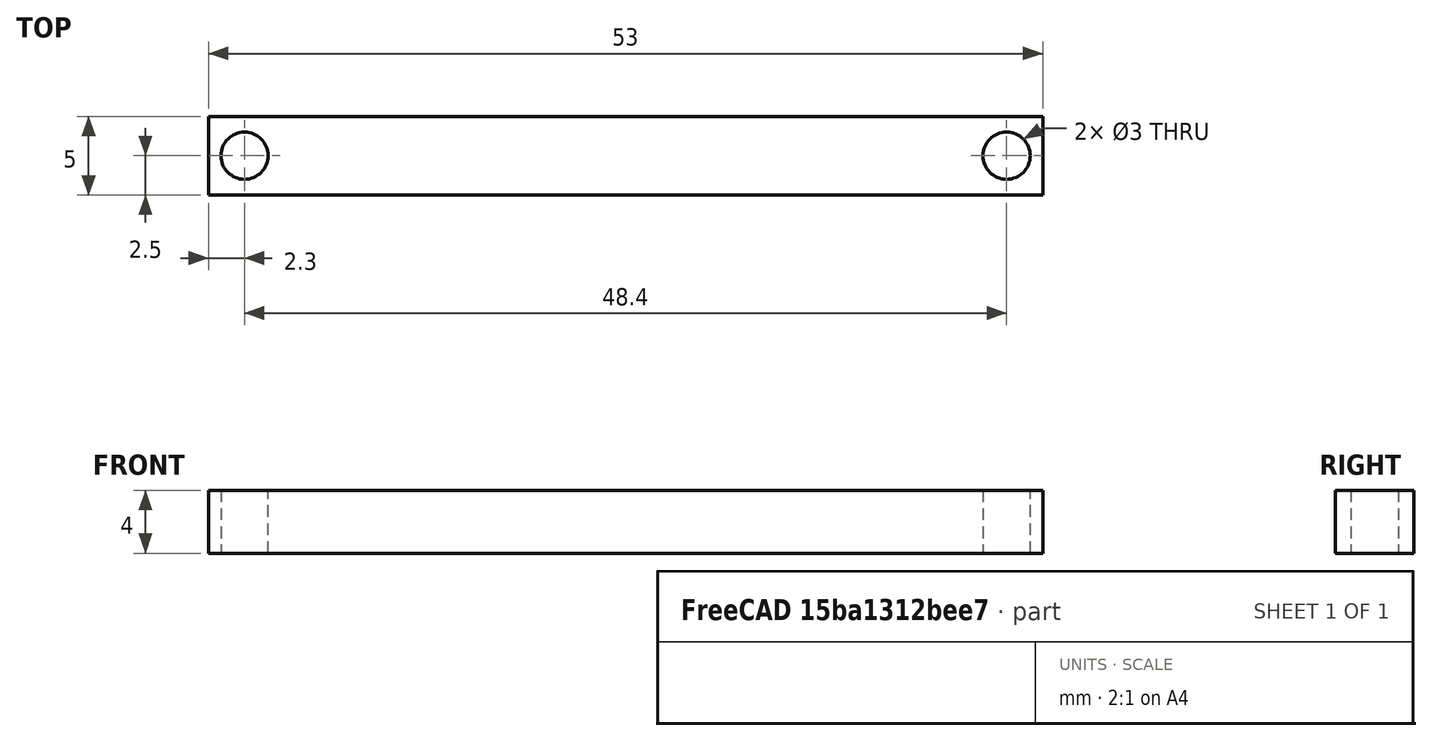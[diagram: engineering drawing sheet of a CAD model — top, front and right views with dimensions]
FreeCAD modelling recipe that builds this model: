
FCSTD DOCUMENT  (FreeCAD 0.20R)
Label: soporte tornillos arduino 2
License: All rights reserved
LicenseURL: http://en.wikipedia.org/wiki/All_rights_reserved
objects: Sketcher::SketchObject×1, PartDesign::Pad×1, PartDesign::Body×1
note: 4 computed .brp shape members not serialized (recipe doc carries the construction recipe); baked Part::Feature solids carry a one-line shape summary decoded from their .brp

FEATURE [Sketcher::SketchObject] Sketch
  FullyConstrained = true
  MapMode = 5
  Support = -> [XY_Plane]
  sketch-geometry (10):
    g0: Circle CenterX=-24.2 CenterY=0 CenterZ=0 NormalX=0 NormalY=0 NormalZ=1 AngleXU=0 Radius=1.5
    g1: Circle CenterX=24.2 CenterY=0 CenterZ=0 NormalX=0 NormalY=0 NormalZ=1 AngleXU=0 Radius=1.5
    g2: LineSegment StartX=-24.2 StartY=0 StartZ=0 EndX=0 EndY=0 EndZ=0
    g3: LineSegment StartX=0 StartY=0 StartZ=0 EndX=24.2 EndY=0 EndZ=0
    g4: LineSegment StartX=-26.5 StartY=2.5 StartZ=0 EndX=26.5 EndY=2.5 EndZ=0
    g5: LineSegment StartX=26.5 StartY=2.5 StartZ=0 EndX=26.5 EndY=-2.5 EndZ=0
    g6: LineSegment StartX=26.5 StartY=-2.5 StartZ=0 EndX=-26.5 EndY=-2.5 EndZ=0
    g7: LineSegment StartX=-26.5 StartY=-2.5 StartZ=0 EndX=-26.5 EndY=2.5 EndZ=0
    g8: LineSegment StartX=-26.5 StartY=2.5 StartZ=0 EndX=0 EndY=0 EndZ=0
    g9: LineSegment StartX=0 StartY=0 StartZ=0 EndX=26.5 EndY=-2.5 EndZ=0
  constraints (26):
    c: PointOnObject(g0,g-1)
    c: PointOnObject(g1,g-1)
    c: Equal(g0,g1)
    c: Coincident(g2,g0)
    c: Coincident(g2,g-1)
    c: Coincident(g3,g-1)
    c: Coincident(g3,g1)
    c: Equal(g3,g2)
    c: DistanceX(g0,g1) = 48.4
    c: Diameter(g1) = 3
    c: Coincident(g4,g5)
    c: Coincident(g5,g6)
    c: Coincident(g6,g7)
    c: Coincident(g7,g4)
    c: Horizontal(g4)
    c: Horizontal(g6)
    c: Vertical(g5)
    c: Vertical(g7)
    c: Coincident(g8,g4)
    c: Coincident(g8,g-1)
    c: Coincident(g9,g-1)
    c: Coincident(g9,g5)
    c: Equal(g9,g8)
    c: Parallel(g8,g9)
    c: DistanceX(g6,g5) = 53
    c: DistanceY(g7,g7) = 5
FEATURE [PartDesign::Pad] Pad
  Direction = (0,0,1)
  Length = 4
  Length2 = 100
  Profile = -> Sketch
  ReferenceAxis = -> Sketch [N_Axis]
  Type = 0
FEATURE [PartDesign::Body] Body
  Group = -> [Sketch,Pad]
  Origin = -> Origin
  Tip = -> Pad
